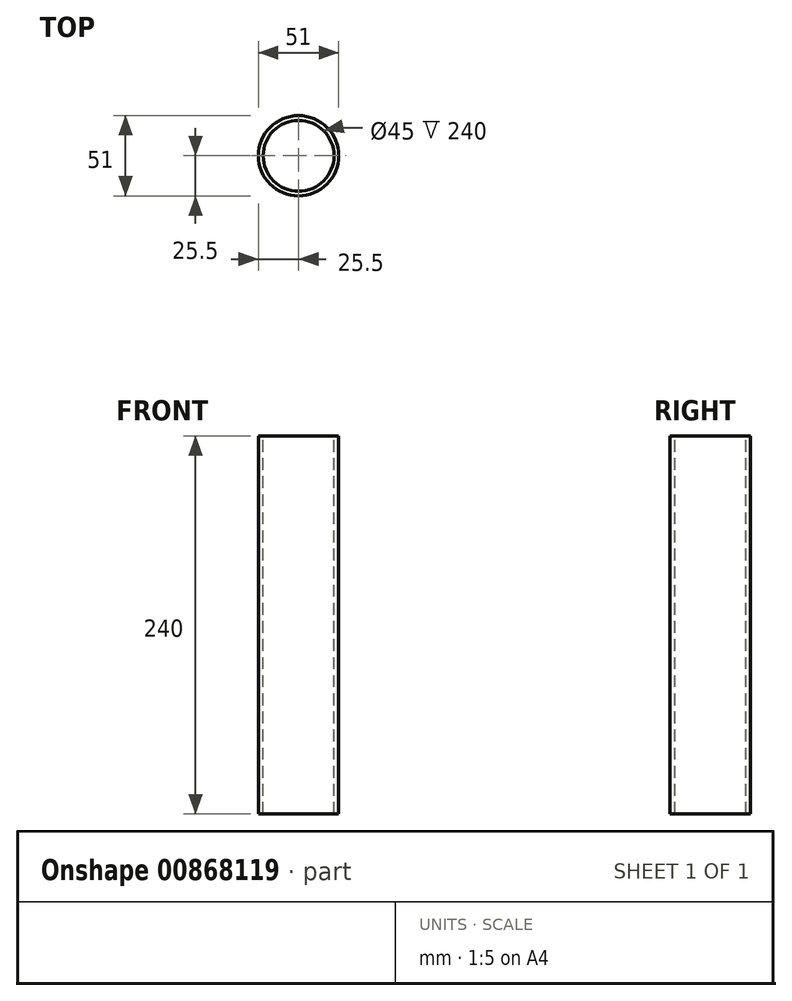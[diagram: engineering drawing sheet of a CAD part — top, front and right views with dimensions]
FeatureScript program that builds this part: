
annotation { "Feature Type Name" : "Feature", "Feature Type Description" : "" }
export const myFeature = defineFeature(function(context is Context, id is Id, definition is map)
    precondition{}
    {
        {
            var Q0;
            Q0=qCreatedBy(makeId("Front.planeOp"),FACE);
            var sketch = newSketch(context, id + "F0", { "sketchPlane" : qUnion([Q0])});
            skLineSegment(sketch, "E0.bottom", {"start": v(-25.5, 100) * mm, "end": v(-22.5, 100) * mm});
            skLineSegment(sketch, "E0.top", {"start": v(-25.5, -140) * mm, "end": v(-22.5, -140) * mm});
            skLineSegment(sketch, "E0.left", {"start": v(-25.5, 100) * mm, "end": v(-25.5, -140) * mm});
            skLineSegment(sketch, "E0.right", {"start": v(-22.5, 100) * mm, "end": v(-22.5, -140) * mm});
            skLineSegment(sketch, "E1", {"start": v(0, 145.8) * mm, "end": v(0, -140.22) * mm, "construction": true});
            skSolve(sketch);
        }
        {
            var Q0;
            Q0 = qSketchRegion(id + "F0", true);
            var Q1;
            Q1=sQuery(id+"F0.wireOp",EDGE,"E1");
            revolve(context, id + "F1", {"surfaceOperationType" : NewSurfaceOperationType.NEW, "entities" : qUnion([Q0]), "axis" : qUnion([Q1]), "revolveType" : RevolveType.FULL});
        }
    });
